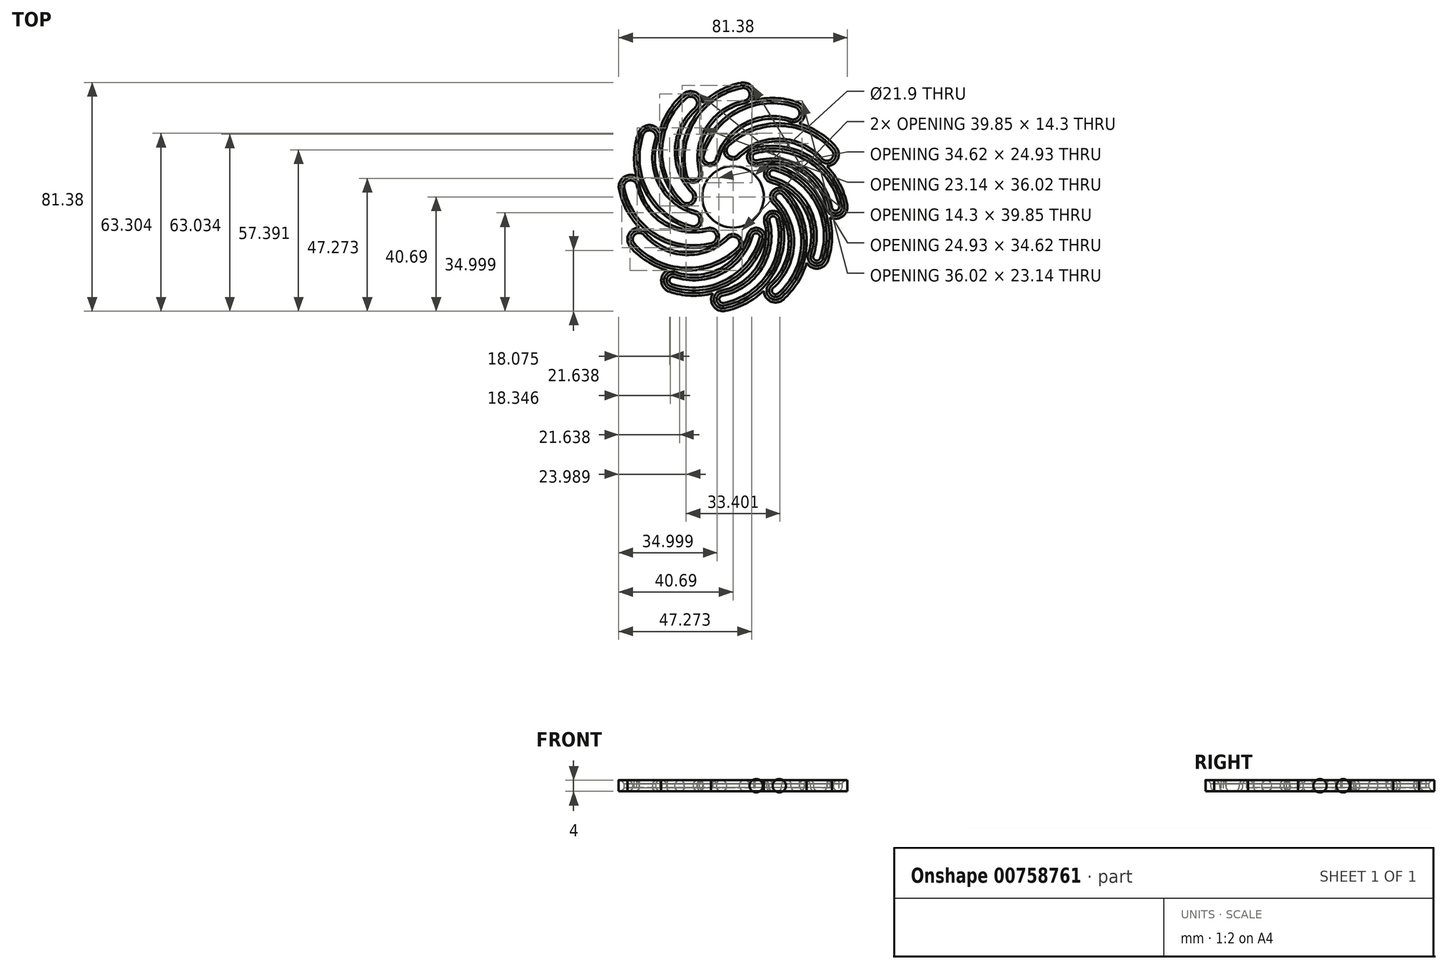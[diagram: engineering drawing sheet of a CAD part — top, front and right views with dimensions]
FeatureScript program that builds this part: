
annotation { "Feature Type Name" : "Feature", "Feature Type Description" : "" }
export const myFeature = defineFeature(function(context is Context, id is Id, definition is map)
    precondition{}
    {
        {
            var Q0;
            Q0=qCreatedBy(makeId("Top.planeOp"),FACE);
            var sketch = newSketch(context, id + "F0", { "sketchPlane" : qUnion([Q0])});
            skArc(sketch, "E0", {"start": v(6.97, 8.45) * mm, "mid": v(0, 10.95) * mm, "end": v(-6.97, 8.45) * mm});
            skPoint(sketch, "E1", {"position": v(0, -24.5) * mm});
            skLineSegment(sketch, "E2", {"start": v(0, 0) * mm, "end": v(0, 16.45) * mm, "construction": true});
            skArc(sketch, "E3", {"start": v(30.24, 12.36) * mm, "mid": v(14.66, 18.75) * mm, "end": v(0.22, 10.1) * mm});
            skArc(sketch, "E4.0", {"start": v(33.4, 15.12) * mm, "mid": v(17, 22.98) * mm, "end": v(0, 16.45) * mm});
            skArc(sketch, "E5.0", {"start": v(36.57, 17.88) * mm, "mid": v(17.06, 27.18) * mm, "end": v(-3.07, 19.32) * mm});
            skArc(sketch, "E6", {"start": v(30.24, 12.36) * mm, "mid": v(36.17, 11.95) * mm, "end": v(36.57, 17.88) * mm});
            skLineSegment(sketch, "E7", {"start": v(-6.97, 8.45) * mm, "end": v(-3.07, 19.32) * mm});
            skArc(sketch, "E8.0", {"start": v(10.47, 12.69) * mm, "mid": v(0, 16.45) * mm, "end": v(-10.47, 12.69) * mm, "construction": true});
            skSolve(sketch);
        }
        {
            var Q0;
            {var subQ4=sQuery(id+"F0.wireOp",EDGE,"PiiM7Q08-lsxY-islm-UEzh-ksM0SnnuY6FK");Q0=makeQuery(id+"F0.imprint","IMPRINT",FACE,{"disambiguationData":[TD([[makeQuery(id+"F0.imprint","IMPRINT",EDGE,{"derivedFrom":subQ4}),-1.0]])]});}
            var Q1;
            Q1=makeQuery(id+"F0.imprint","IMPRINT",FACE,{"disambiguationData":[TD([[makeQuery(id+"F0.imprint","IMPRINT",EDGE,{"derivedFrom":sQuery(id+"F0.wireOp",EDGE,"E0")}),-1.0]])]});
            var Q2;
            {var subQ4=sQuery(id+"F0.wireOp",EDGE,"QqK0a54Q-URX9-TbrE-nkqz-KXdzGL0UVco7");Q2=makeQuery(id+"F0.imprint","IMPRINT",FACE,{"disambiguationData":[TD([[makeQuery(id+"F0.imprint","IMPRINT",EDGE,{"derivedFrom":subQ4}),-1.0]])]});}
            var Q3;
            {var subQ5=sQuery(id+"F0.wireOp",EDGE,"PiiM7Q08-lsxY-islm-UEzh-ksM0SnnuY6FK");Q3=makeQuery(id+"F0.imprint","IMPRINT",FACE,{"disambiguationData":[TD([[makeQuery(id+"F0.imprint","IMPRINT",EDGE,{"derivedFrom":subQ5}),1.0]])]});}
            var Q4;
            {var subQ1=sQuery(id+"F0.wireOp",EDGE,"E5.0");Q4=makeQuery(id+"F0.imprint","IMPRINT",FACE,{"disambiguationData":[TD([[makeQuery(id+"F0.imprint","IMPRINT",EDGE,{"derivedFrom":subQ1}),1.0]])]});}
            extrude(context, id + "F1", {"entities" : qUnion([Q0, Q1, Q2, Q3, Q4]), "endBound" : BoundingType.SYMMETRIC, "depth" : 4 * mm, "offsetDistance" : 25 * mm});
        }
        {
            var Q0;
            Q0=makeQuery(id+"F1.opExtrude","SWEPT_EDGE",EDGE,{"disambiguationData":[OSD([sQuery(id+"F0.wireOp",EDGE,"E3"),sQuery(id+"F0.wireOp",EDGE,"E6")])]});
            var Q1;
            Q1=sQuery(id+"F0.wireOp",VERTEX,"E5.0.start");
            cPlane(context, id + "F2", {"entities" : qUnion([Q0, Q1]), "cplaneType" : CPlaneType.LINE_ANGLE, "offset" : 25 * mm, "angle" : 0 * degree, "width" : 150 * mm, "height" : 150 * mm});
        }
        {
            var Q0;
            Q0=qCreatedBy(id+"F2.planeOp",FACE);
            var sketch = newSketch(context, id + "F3", { "sketchPlane" : qUnion([Q0])});
            skLineSegment(sketch, "E9", {"start": v(35.11, 2.38) * mm, "end": v(35.11, -2.38) * mm});
            skArc(sketch, "E10", {"start": v(35.11, -2.38) * mm, "mid": v(37.49, 0) * mm, "end": v(35.11, 2.38) * mm});
            skArc(sketch, "E11.MirrorCS", {"start": v(35.11, -2.38) * mm, "mid": v(32.74, 0) * mm, "end": v(35.11, 2.38) * mm});
            skSolve(sketch);
        }
        {
            var Q0;
            Q0=makeQuery(id+"F3.imprint","IMPRINT",FACE,{"disambiguationData":[TD([[makeQuery(id+"F3.imprint","IMPRINT",EDGE,{"derivedFrom":sQuery(id+"F3.wireOp",EDGE,"E9")}),1.0]])]});
            var Q1;
            Q1=makeQuery(id+"F3.imprint","IMPRINT",FACE,{"disambiguationData":[TD([[makeQuery(id+"F3.imprint","IMPRINT",EDGE,{"derivedFrom":sQuery(id+"F3.wireOp",EDGE,"E9")}),-1.0]])]});
            var Q2;
            Q2=sQuery(id+"F0.wireOp",EDGE,"E4.0");
            sweep(context, id + "F4", {"operationType" : NewBodyOperationType.REMOVE, "profiles" : qUnion([Q0, Q1]), "path" : qUnion([Q2])});
        }
        {
            var Q0;
            Q0=makeQuery(id+"F3.imprint","IMPRINT",FACE,{"disambiguationData":[TD([[makeQuery(id+"F3.imprint","IMPRINT",EDGE,{"derivedFrom":sQuery(id+"F3.wireOp",EDGE,"E9")}),1.0]])]});
            var Q1;
            Q1=sQuery(id+"F3.wireOp",EDGE,"E9");
            revolve(context, id + "F5", {"operationType" : NewBodyOperationType.REMOVE, "surfaceOperationType" : NewSurfaceOperationType.NEW, "entities" : qUnion([Q0]), "axis" : qUnion([Q1]), "revolveType" : RevolveType.ONE_DIRECTION, "angle" : 180 * degree});
        }
        {
            var Q0;
            Q0=makeQuery(id+"F4.boolean.opBoolean","COPY",FACE,{"derivedFrom":makeQuery(id+"F4.opSweep","CAP_FACE",FACE,{"disambiguationData":[OSD([sQuery(id+"F0.wireOp",VERTEX,"E4.0.end"),sQuery(id+"F3.wireOp",EDGE,"E10"),sQuery(id+"F3.wireOp",EDGE,"E11.MirrorCS")])],"isStart":false})});
            var sketch = newSketch(context, id + "F6", { "sketchPlane" : qUnion([Q0])});
            skLineSegment(sketch, "E12", {"start": v(14.14, 0) * mm, "end": v(9.4, 0) * mm});
            skArc(sketch, "E13", {"start": v(9.4, 0) * mm, "mid": v(11.77, -2.37) * mm, "end": v(14.14, 0) * mm});
            skSolve(sketch);
        }
        {
            var Q0;
            {var subQ1=makeQuery(id+"F4.boolean.opBoolean","INTERSECT",EDGE,{"derivedFrom":[makeQuery(id+"F1.opExtrude","CAP_FACE",FACE,{"disambiguationData":[OSD([sQuery(id+"F0.wireOp",EDGE,"E0"),sQuery(id+"F0.wireOp",EDGE,"Lb8NWhK4-ym9p-KzVv-z8Fr-7k6zUVGv0M9w"),sQuery(id+"F0.wireOp",EDGE,"QqK0a54Q-URX9-TbrE-nkqz-KXdzGL0UVco7"),sQuery(id+"F0.wireOp",EDGE,"E3"),sQuery(id+"F0.wireOp",EDGE,"E5.0"),sQuery(id+"F0.wireOp",EDGE,"E6"),sQuery(id+"F0.wireOp",EDGE,"E7")])],"isStart":true}),makeQuery(id+"F4.opSweep","CAP_FACE",FACE,{"disambiguationData":[OSD([sQuery(id+"F0.wireOp",VERTEX,"I2wmlmdm-DSrS-oub0-GOcV-EtuJTHkaWZzk.end"),sQuery(id+"F3.wireOp",EDGE,"E10"),sQuery(id+"F3.wireOp",EDGE,"E11.MirrorCS")])],"isStart":false})]});Q0=makeQuery(id+"F6.imprint","IMPRINT",FACE,{"disambiguationData":[TD([[makeQuery(id+"F6.imprint","IMPRINT",EDGE,{"derivedFrom":subQ1}),-1.0]])]});}
            var Q1;
            {var subQ0=sQuery(id+"F6.wireOp",EDGE,"E12");Q1=makeQuery(id+"F6.imprint","IMPRINT",FACE,{"disambiguationData":[TD([[makeQuery(id+"F6.imprint","IMPRINT",EDGE,{"derivedFrom":subQ0}),1.0]])]});}
            var Q2;
            Q2=sQuery(id+"F6.wireOp",EDGE,"E12");
            revolve(context, id + "F7", {"operationType" : NewBodyOperationType.REMOVE, "surfaceOperationType" : NewSurfaceOperationType.NEW, "entities" : qUnion([Q0, Q1]), "axis" : qUnion([Q2]), "revolveType" : RevolveType.FULL, "oppositeDirection" : true});
        }
        {
            var Q0;
            Q0=qCreatedBy(makeId("Front.planeOp"),FACE);
            var sketch = newSketch(context, id + "F8", { "sketchPlane" : qUnion([Q0])});
            skLineSegment(sketch, "E14", {"start": v(0, -9.37) * mm, "end": v(0, 10.86) * mm, "construction": true});
            skSolve(sketch);
        }
        {
            var Q0;
            Q0=makeQuery(id+"F1.opExtrude","SWEPT_BODY",BODY,{"disambiguationData":[OSD([sQuery(id+"F0.wireOp",EDGE,"E0"),sQuery(id+"F0.wireOp",EDGE,"Lb8NWhK4-ym9p-KzVv-z8Fr-7k6zUVGv0M9w"),sQuery(id+"F0.wireOp",EDGE,"QqK0a54Q-URX9-TbrE-nkqz-KXdzGL0UVco7"),sQuery(id+"F0.wireOp",EDGE,"E3"),sQuery(id+"F0.wireOp",EDGE,"E5.0"),sQuery(id+"F0.wireOp",EDGE,"E6"),sQuery(id+"F0.wireOp",EDGE,"E7")])]});
            var Q1;
            Q1=sQuery(id+"F8.wireOp",EDGE,"E14");
            circularPattern(context, id + "F9", {"operationType" : NewBodyOperationType.ADD, "entities" : qUnion([Q0]), "axis" : qUnion([Q1]), "angle" : 360 * degree, "instanceCount" : 12, "equalSpace" : true});
        }
        {
            var Q0;
            Q0=makeQuery(id+"F9.opPattern","COPY",EDGE,{"derivedFrom":makeQuery(id+"F4.boolean.opBoolean","INTERSECT",EDGE,{"disambiguationData":[OD(1.0)],"derivedFrom":[makeQuery(id+"F1.opExtrude","CAP_FACE",FACE,{"disambiguationData":[OSD([sQuery(id+"F0.wireOp",EDGE,"E0"),sQuery(id+"F0.wireOp",EDGE,"E3"),sQuery(id+"F0.wireOp",EDGE,"E5.0"),sQuery(id+"F0.wireOp",EDGE,"E6"),sQuery(id+"F0.wireOp",EDGE,"E7")])],"isStart":false}),makeQuery(id+"F4.opSweep","SWEPT_FACE",FACE,{"disambiguationData":[OSD([sQuery(id+"F0.wireOp",EDGE,"E4.0"),sQuery(id+"F3.wireOp",EDGE,"E10"),sQuery(id+"F3.wireOp",EDGE,"E11.MirrorCS")])]})]}),"instanceName":"3"});
            var Q1;
            Q1=makeQuery(id+"F9.opPattern","COPY",EDGE,{"derivedFrom":makeQuery(id+"F4.boolean.opBoolean","INTERSECT",EDGE,{"disambiguationData":[OD(0.0)],"derivedFrom":[makeQuery(id+"F1.opExtrude","CAP_FACE",FACE,{"disambiguationData":[OSD([sQuery(id+"F0.wireOp",EDGE,"E0"),sQuery(id+"F0.wireOp",EDGE,"E3"),sQuery(id+"F0.wireOp",EDGE,"E5.0"),sQuery(id+"F0.wireOp",EDGE,"E6"),sQuery(id+"F0.wireOp",EDGE,"E7")])],"isStart":false}),makeQuery(id+"F4.opSweep","SWEPT_FACE",FACE,{"disambiguationData":[OSD([sQuery(id+"F0.wireOp",EDGE,"E4.0"),sQuery(id+"F3.wireOp",EDGE,"E10"),sQuery(id+"F3.wireOp",EDGE,"E11.MirrorCS")])]})]}),"instanceName":"4"});
            var Q2;
            Q2=makeQuery(id+"F9.opPattern","COPY",EDGE,{"derivedFrom":makeQuery(id+"F4.boolean.opBoolean","INTERSECT",EDGE,{"disambiguationData":[OD(1.0)],"derivedFrom":[makeQuery(id+"F1.opExtrude","CAP_FACE",FACE,{"disambiguationData":[OSD([sQuery(id+"F0.wireOp",EDGE,"E0"),sQuery(id+"F0.wireOp",EDGE,"E3"),sQuery(id+"F0.wireOp",EDGE,"E5.0"),sQuery(id+"F0.wireOp",EDGE,"E6"),sQuery(id+"F0.wireOp",EDGE,"E7")])],"isStart":false}),makeQuery(id+"F4.opSweep","SWEPT_FACE",FACE,{"disambiguationData":[OSD([sQuery(id+"F0.wireOp",EDGE,"E4.0"),sQuery(id+"F3.wireOp",EDGE,"E10"),sQuery(id+"F3.wireOp",EDGE,"E11.MirrorCS")])]})]}),"instanceName":"5"});
            var Q3;
            Q3=makeQuery(id+"F9.opPattern","COPY",EDGE,{"derivedFrom":makeQuery(id+"F4.boolean.opBoolean","INTERSECT",EDGE,{"disambiguationData":[OD(0.0)],"derivedFrom":[makeQuery(id+"F1.opExtrude","CAP_FACE",FACE,{"disambiguationData":[OSD([sQuery(id+"F0.wireOp",EDGE,"E0"),sQuery(id+"F0.wireOp",EDGE,"E3"),sQuery(id+"F0.wireOp",EDGE,"E5.0"),sQuery(id+"F0.wireOp",EDGE,"E6"),sQuery(id+"F0.wireOp",EDGE,"E7")])],"isStart":false}),makeQuery(id+"F4.opSweep","SWEPT_FACE",FACE,{"disambiguationData":[OSD([sQuery(id+"F0.wireOp",EDGE,"E4.0"),sQuery(id+"F3.wireOp",EDGE,"E10"),sQuery(id+"F3.wireOp",EDGE,"E11.MirrorCS")])]})]}),"instanceName":"6"});
            var Q4;
            Q4=makeQuery(id+"F4.boolean.opBoolean","INTERSECT",EDGE,{"disambiguationData":[OD(0.0)],"derivedFrom":[makeQuery(id+"F1.opExtrude","CAP_FACE",FACE,{"disambiguationData":[OSD([sQuery(id+"F0.wireOp",EDGE,"E0"),sQuery(id+"F0.wireOp",EDGE,"E3"),sQuery(id+"F0.wireOp",EDGE,"E5.0"),sQuery(id+"F0.wireOp",EDGE,"E6"),sQuery(id+"F0.wireOp",EDGE,"E7")])],"isStart":false}),makeQuery(id+"F4.opSweep","SWEPT_FACE",FACE,{"disambiguationData":[OSD([sQuery(id+"F0.wireOp",EDGE,"E4.0"),sQuery(id+"F3.wireOp",EDGE,"E10"),sQuery(id+"F3.wireOp",EDGE,"E11.MirrorCS")])]})]});
            var Q5;
            Q5=makeQuery(id+"F9.opPattern","COPY",EDGE,{"derivedFrom":makeQuery(id+"F4.boolean.opBoolean","INTERSECT",EDGE,{"disambiguationData":[OD(0.0)],"derivedFrom":[makeQuery(id+"F1.opExtrude","CAP_FACE",FACE,{"disambiguationData":[OSD([sQuery(id+"F0.wireOp",EDGE,"E0"),sQuery(id+"F0.wireOp",EDGE,"E3"),sQuery(id+"F0.wireOp",EDGE,"E5.0"),sQuery(id+"F0.wireOp",EDGE,"E6"),sQuery(id+"F0.wireOp",EDGE,"E7")])],"isStart":false}),makeQuery(id+"F4.opSweep","SWEPT_FACE",FACE,{"disambiguationData":[OSD([sQuery(id+"F0.wireOp",EDGE,"E4.0"),sQuery(id+"F3.wireOp",EDGE,"E10"),sQuery(id+"F3.wireOp",EDGE,"E11.MirrorCS")])]})]}),"instanceName":"1"});
            var Q6;
            Q6=makeQuery(id+"F9.opPattern","COPY",EDGE,{"derivedFrom":makeQuery(id+"F4.boolean.opBoolean","INTERSECT",EDGE,{"disambiguationData":[OD(0.0)],"derivedFrom":[makeQuery(id+"F1.opExtrude","CAP_FACE",FACE,{"disambiguationData":[OSD([sQuery(id+"F0.wireOp",EDGE,"E0"),sQuery(id+"F0.wireOp",EDGE,"E3"),sQuery(id+"F0.wireOp",EDGE,"E5.0"),sQuery(id+"F0.wireOp",EDGE,"E6"),sQuery(id+"F0.wireOp",EDGE,"E7")])],"isStart":false}),makeQuery(id+"F4.opSweep","SWEPT_FACE",FACE,{"disambiguationData":[OSD([sQuery(id+"F0.wireOp",EDGE,"E4.0"),sQuery(id+"F3.wireOp",EDGE,"E10"),sQuery(id+"F3.wireOp",EDGE,"E11.MirrorCS")])]})]}),"instanceName":"2"});
            var Q7;
            Q7=makeQuery(id+"F9.opPattern","COPY",EDGE,{"derivedFrom":makeQuery(id+"F4.boolean.opBoolean","INTERSECT",EDGE,{"disambiguationData":[OD(1.0)],"derivedFrom":[makeQuery(id+"F1.opExtrude","CAP_FACE",FACE,{"disambiguationData":[OSD([sQuery(id+"F0.wireOp",EDGE,"E0"),sQuery(id+"F0.wireOp",EDGE,"E3"),sQuery(id+"F0.wireOp",EDGE,"E5.0"),sQuery(id+"F0.wireOp",EDGE,"E6"),sQuery(id+"F0.wireOp",EDGE,"E7")])],"isStart":true}),makeQuery(id+"F4.opSweep","SWEPT_FACE",FACE,{"disambiguationData":[OSD([sQuery(id+"F0.wireOp",EDGE,"E4.0"),sQuery(id+"F3.wireOp",EDGE,"E10"),sQuery(id+"F3.wireOp",EDGE,"E11.MirrorCS")])]})]}),"instanceName":"4"});
            var Q8;
            Q8=makeQuery(id+"F9.opPattern","COPY",EDGE,{"derivedFrom":makeQuery(id+"F4.boolean.opBoolean","INTERSECT",EDGE,{"disambiguationData":[OD(0.0)],"derivedFrom":[makeQuery(id+"F1.opExtrude","CAP_FACE",FACE,{"disambiguationData":[OSD([sQuery(id+"F0.wireOp",EDGE,"E0"),sQuery(id+"F0.wireOp",EDGE,"E3"),sQuery(id+"F0.wireOp",EDGE,"E5.0"),sQuery(id+"F0.wireOp",EDGE,"E6"),sQuery(id+"F0.wireOp",EDGE,"E7")])],"isStart":true}),makeQuery(id+"F4.opSweep","SWEPT_FACE",FACE,{"disambiguationData":[OSD([sQuery(id+"F0.wireOp",EDGE,"E4.0"),sQuery(id+"F3.wireOp",EDGE,"E10"),sQuery(id+"F3.wireOp",EDGE,"E11.MirrorCS")])]})]}),"instanceName":"5"});
            var Q9;
            Q9=makeQuery(id+"F9.opPattern","COPY",EDGE,{"derivedFrom":makeQuery(id+"F4.boolean.opBoolean","INTERSECT",EDGE,{"disambiguationData":[OD(0.0)],"derivedFrom":[makeQuery(id+"F1.opExtrude","CAP_FACE",FACE,{"disambiguationData":[OSD([sQuery(id+"F0.wireOp",EDGE,"E0"),sQuery(id+"F0.wireOp",EDGE,"E3"),sQuery(id+"F0.wireOp",EDGE,"E5.0"),sQuery(id+"F0.wireOp",EDGE,"E6"),sQuery(id+"F0.wireOp",EDGE,"E7")])],"isStart":true}),makeQuery(id+"F4.opSweep","SWEPT_FACE",FACE,{"disambiguationData":[OSD([sQuery(id+"F0.wireOp",EDGE,"E4.0"),sQuery(id+"F3.wireOp",EDGE,"E10"),sQuery(id+"F3.wireOp",EDGE,"E11.MirrorCS")])]})]}),"instanceName":"6"});
            var Q10;
            Q10=makeQuery(id+"F4.boolean.opBoolean","INTERSECT",EDGE,{"disambiguationData":[OD(0.0)],"derivedFrom":[makeQuery(id+"F1.opExtrude","CAP_FACE",FACE,{"disambiguationData":[OSD([sQuery(id+"F0.wireOp",EDGE,"E0"),sQuery(id+"F0.wireOp",EDGE,"E3"),sQuery(id+"F0.wireOp",EDGE,"E5.0"),sQuery(id+"F0.wireOp",EDGE,"E6"),sQuery(id+"F0.wireOp",EDGE,"E7")])],"isStart":true}),makeQuery(id+"F4.opSweep","SWEPT_FACE",FACE,{"disambiguationData":[OSD([sQuery(id+"F0.wireOp",EDGE,"E4.0"),sQuery(id+"F3.wireOp",EDGE,"E10"),sQuery(id+"F3.wireOp",EDGE,"E11.MirrorCS")])]})]});
            var Q11;
            Q11=makeQuery(id+"F9.opPattern","COPY",EDGE,{"derivedFrom":makeQuery(id+"F4.boolean.opBoolean","INTERSECT",EDGE,{"disambiguationData":[OD(0.0)],"derivedFrom":[makeQuery(id+"F1.opExtrude","CAP_FACE",FACE,{"disambiguationData":[OSD([sQuery(id+"F0.wireOp",EDGE,"E0"),sQuery(id+"F0.wireOp",EDGE,"E3"),sQuery(id+"F0.wireOp",EDGE,"E5.0"),sQuery(id+"F0.wireOp",EDGE,"E6"),sQuery(id+"F0.wireOp",EDGE,"E7")])],"isStart":true}),makeQuery(id+"F4.opSweep","SWEPT_FACE",FACE,{"disambiguationData":[OSD([sQuery(id+"F0.wireOp",EDGE,"E4.0"),sQuery(id+"F3.wireOp",EDGE,"E10"),sQuery(id+"F3.wireOp",EDGE,"E11.MirrorCS")])]})]}),"instanceName":"1"});
            var Q12;
            Q12=makeQuery(id+"F9.opPattern","COPY",EDGE,{"derivedFrom":makeQuery(id+"F4.boolean.opBoolean","INTERSECT",EDGE,{"disambiguationData":[OD(0.0)],"derivedFrom":[makeQuery(id+"F1.opExtrude","CAP_FACE",FACE,{"disambiguationData":[OSD([sQuery(id+"F0.wireOp",EDGE,"E0"),sQuery(id+"F0.wireOp",EDGE,"E3"),sQuery(id+"F0.wireOp",EDGE,"E5.0"),sQuery(id+"F0.wireOp",EDGE,"E6"),sQuery(id+"F0.wireOp",EDGE,"E7")])],"isStart":true}),makeQuery(id+"F4.opSweep","SWEPT_FACE",FACE,{"disambiguationData":[OSD([sQuery(id+"F0.wireOp",EDGE,"E4.0"),sQuery(id+"F3.wireOp",EDGE,"E10"),sQuery(id+"F3.wireOp",EDGE,"E11.MirrorCS")])]})]}),"instanceName":"2"});
            var Q13;
            Q13=makeQuery(id+"F9.opPattern","COPY",EDGE,{"derivedFrom":makeQuery(id+"F4.boolean.opBoolean","INTERSECT",EDGE,{"disambiguationData":[OD(0.0)],"derivedFrom":[makeQuery(id+"F1.opExtrude","CAP_FACE",FACE,{"disambiguationData":[OSD([sQuery(id+"F0.wireOp",EDGE,"E0"),sQuery(id+"F0.wireOp",EDGE,"E3"),sQuery(id+"F0.wireOp",EDGE,"E5.0"),sQuery(id+"F0.wireOp",EDGE,"E6"),sQuery(id+"F0.wireOp",EDGE,"E7")])],"isStart":true}),makeQuery(id+"F4.opSweep","SWEPT_FACE",FACE,{"disambiguationData":[OSD([sQuery(id+"F0.wireOp",EDGE,"E4.0"),sQuery(id+"F3.wireOp",EDGE,"E10"),sQuery(id+"F3.wireOp",EDGE,"E11.MirrorCS")])]})]}),"instanceName":"3"});
            var Q14;
            Q14=makeQuery(id+"F9.opPattern","COPY",EDGE,{"derivedFrom":makeQuery(id+"F4.boolean.opBoolean","INTERSECT",EDGE,{"disambiguationData":[OD(1.0)],"derivedFrom":[makeQuery(id+"F1.opExtrude","CAP_FACE",FACE,{"disambiguationData":[OSD([sQuery(id+"F0.wireOp",EDGE,"E0"),sQuery(id+"F0.wireOp",EDGE,"E3"),sQuery(id+"F0.wireOp",EDGE,"E5.0"),sQuery(id+"F0.wireOp",EDGE,"E6"),sQuery(id+"F0.wireOp",EDGE,"E7")])],"isStart":false}),makeQuery(id+"F4.opSweep","SWEPT_FACE",FACE,{"disambiguationData":[OSD([sQuery(id+"F0.wireOp",EDGE,"E4.0"),sQuery(id+"F3.wireOp",EDGE,"E10"),sQuery(id+"F3.wireOp",EDGE,"E11.MirrorCS")])]})]}),"instanceName":"11"});
            var Q15;
            Q15=makeQuery(id+"F9.opPattern","COPY",EDGE,{"derivedFrom":makeQuery(id+"F4.boolean.opBoolean","INTERSECT",EDGE,{"disambiguationData":[OD(0.0)],"derivedFrom":[makeQuery(id+"F1.opExtrude","CAP_FACE",FACE,{"disambiguationData":[OSD([sQuery(id+"F0.wireOp",EDGE,"E0"),sQuery(id+"F0.wireOp",EDGE,"E3"),sQuery(id+"F0.wireOp",EDGE,"E5.0"),sQuery(id+"F0.wireOp",EDGE,"E6"),sQuery(id+"F0.wireOp",EDGE,"E7")])],"isStart":false}),makeQuery(id+"F4.opSweep","SWEPT_FACE",FACE,{"disambiguationData":[OSD([sQuery(id+"F0.wireOp",EDGE,"E4.0"),sQuery(id+"F3.wireOp",EDGE,"E10"),sQuery(id+"F3.wireOp",EDGE,"E11.MirrorCS")])]})]}),"instanceName":"11"});
            var Q16;
            Q16=makeQuery(id+"F9.opPattern","COPY",EDGE,{"derivedFrom":makeQuery(id+"F7.boolean.opBoolean","INTERSECT",EDGE,{"derivedFrom":[makeQuery(id+"F1.opExtrude","CAP_FACE",FACE,{"disambiguationData":[OSD([sQuery(id+"F0.wireOp",EDGE,"E0"),sQuery(id+"F0.wireOp",EDGE,"E3"),sQuery(id+"F0.wireOp",EDGE,"E5.0"),sQuery(id+"F0.wireOp",EDGE,"E6"),sQuery(id+"F0.wireOp",EDGE,"E7")])],"isStart":false}),makeQuery(id+"F7.opRevolve","SWEPT_FACE",FACE,{"disambiguationData":[OSD([sQuery(id+"F6.wireOp",EDGE,"E13")])]})]}),"instanceName":"11"});
            var Q17;
            Q17=makeQuery(id+"F9.opPattern","COPY",EDGE,{"derivedFrom":makeQuery(id+"F4.boolean.opBoolean","INTERSECT",EDGE,{"disambiguationData":[OD(0.0)],"derivedFrom":[makeQuery(id+"F1.opExtrude","CAP_FACE",FACE,{"disambiguationData":[OSD([sQuery(id+"F0.wireOp",EDGE,"E0"),sQuery(id+"F0.wireOp",EDGE,"E3"),sQuery(id+"F0.wireOp",EDGE,"E5.0"),sQuery(id+"F0.wireOp",EDGE,"E6"),sQuery(id+"F0.wireOp",EDGE,"E7")])],"isStart":false}),makeQuery(id+"F4.opSweep","SWEPT_FACE",FACE,{"disambiguationData":[OSD([sQuery(id+"F0.wireOp",EDGE,"E4.0"),sQuery(id+"F3.wireOp",EDGE,"E10"),sQuery(id+"F3.wireOp",EDGE,"E11.MirrorCS")])]})]}),"instanceName":"10"});
            var Q18;
            Q18=makeQuery(id+"F9.opPattern","COPY",EDGE,{"derivedFrom":makeQuery(id+"F4.boolean.opBoolean","INTERSECT",EDGE,{"disambiguationData":[OD(1.0)],"derivedFrom":[makeQuery(id+"F1.opExtrude","CAP_FACE",FACE,{"disambiguationData":[OSD([sQuery(id+"F0.wireOp",EDGE,"E0"),sQuery(id+"F0.wireOp",EDGE,"E3"),sQuery(id+"F0.wireOp",EDGE,"E5.0"),sQuery(id+"F0.wireOp",EDGE,"E6"),sQuery(id+"F0.wireOp",EDGE,"E7")])],"isStart":false}),makeQuery(id+"F4.opSweep","SWEPT_FACE",FACE,{"disambiguationData":[OSD([sQuery(id+"F0.wireOp",EDGE,"E4.0"),sQuery(id+"F3.wireOp",EDGE,"E10"),sQuery(id+"F3.wireOp",EDGE,"E11.MirrorCS")])]})]}),"instanceName":"9"});
            var Q19;
            Q19=makeQuery(id+"F9.opPattern","COPY",EDGE,{"derivedFrom":makeQuery(id+"F4.boolean.opBoolean","INTERSECT",EDGE,{"disambiguationData":[OD(1.0)],"derivedFrom":[makeQuery(id+"F1.opExtrude","CAP_FACE",FACE,{"disambiguationData":[OSD([sQuery(id+"F0.wireOp",EDGE,"E0"),sQuery(id+"F0.wireOp",EDGE,"E3"),sQuery(id+"F0.wireOp",EDGE,"E5.0"),sQuery(id+"F0.wireOp",EDGE,"E6"),sQuery(id+"F0.wireOp",EDGE,"E7")])],"isStart":false}),makeQuery(id+"F4.opSweep","SWEPT_FACE",FACE,{"disambiguationData":[OSD([sQuery(id+"F0.wireOp",EDGE,"E4.0"),sQuery(id+"F3.wireOp",EDGE,"E10"),sQuery(id+"F3.wireOp",EDGE,"E11.MirrorCS")])]})]}),"instanceName":"8"});
            var Q20;
            Q20=makeQuery(id+"F9.opPattern","COPY",EDGE,{"derivedFrom":makeQuery(id+"F4.boolean.opBoolean","INTERSECT",EDGE,{"disambiguationData":[OD(1.0)],"derivedFrom":[makeQuery(id+"F1.opExtrude","CAP_FACE",FACE,{"disambiguationData":[OSD([sQuery(id+"F0.wireOp",EDGE,"E0"),sQuery(id+"F0.wireOp",EDGE,"E3"),sQuery(id+"F0.wireOp",EDGE,"E5.0"),sQuery(id+"F0.wireOp",EDGE,"E6"),sQuery(id+"F0.wireOp",EDGE,"E7")])],"isStart":false}),makeQuery(id+"F4.opSweep","SWEPT_FACE",FACE,{"disambiguationData":[OSD([sQuery(id+"F0.wireOp",EDGE,"E4.0"),sQuery(id+"F3.wireOp",EDGE,"E10"),sQuery(id+"F3.wireOp",EDGE,"E11.MirrorCS")])]})]}),"instanceName":"7"});
            chamfer(context, id + "F10", {"entities" : qUnion([Q0, Q1, Q2, Q3, Q4, Q5, Q6, Q7, Q8, Q9, Q10, Q11, Q12, Q13, Q14, Q15, Q16, Q17, Q18, Q19, Q20]), "width" : 1 * mm, "tangentPropagation" : true});
        }
    });
